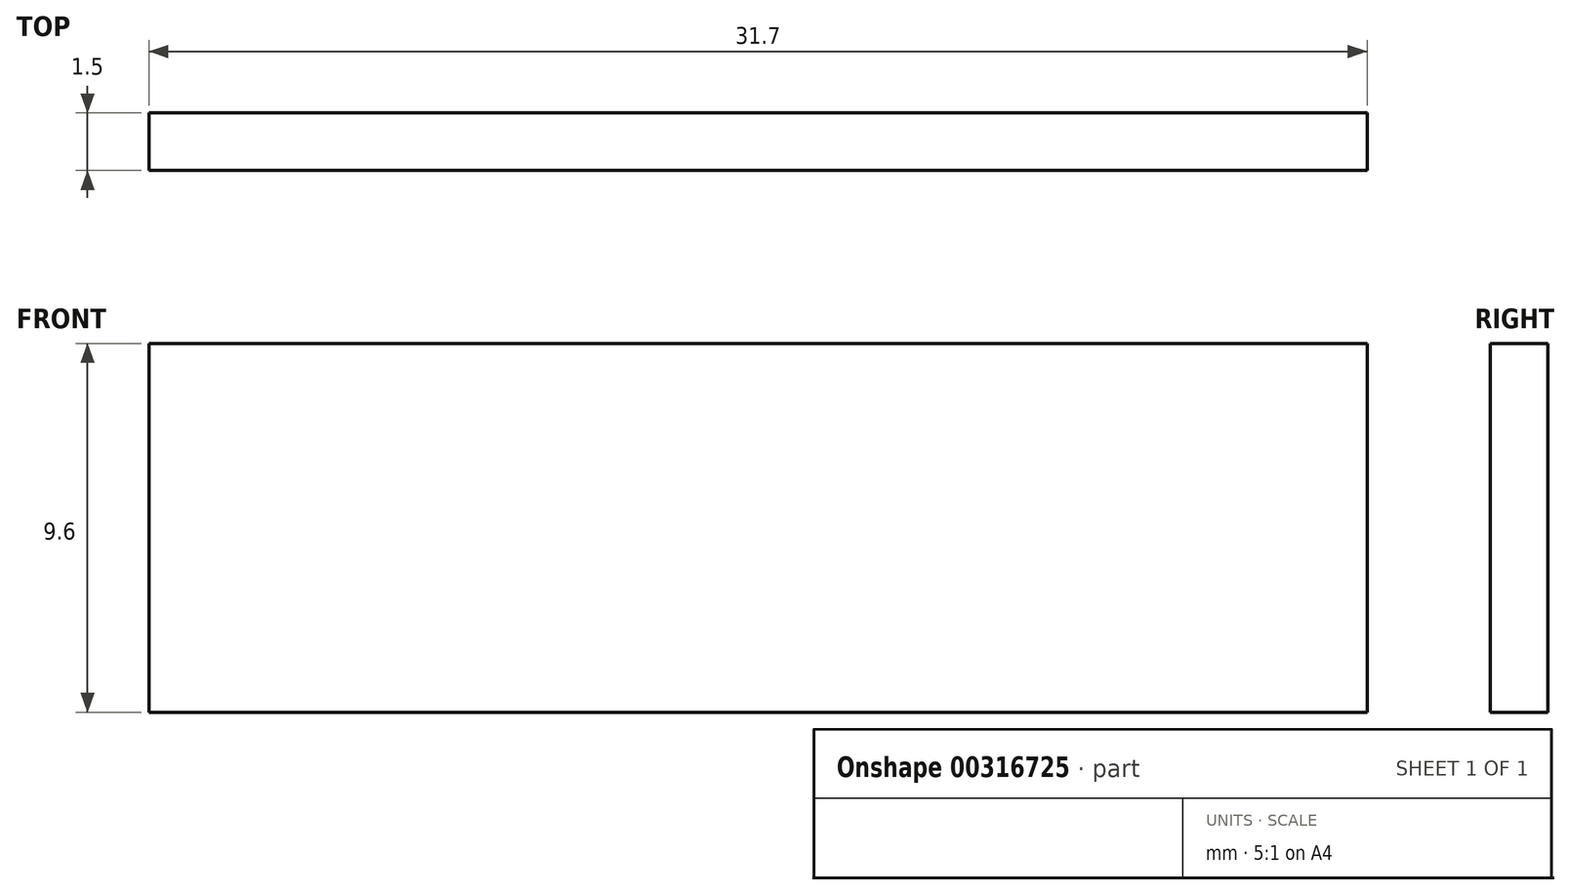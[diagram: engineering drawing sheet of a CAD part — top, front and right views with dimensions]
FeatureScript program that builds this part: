
annotation { "Feature Type Name" : "Feature", "Feature Type Description" : "" }
export const myFeature = defineFeature(function(context is Context, id is Id, definition is map)
    precondition{}
    {
        {
            var Q0;
            Q0=qCreatedBy(makeId("Front.planeOp"),FACE);
            var sketch = newSketch(context, id + "F0", { "sketchPlane" : qUnion([Q0])});
            skLineSegment(sketch, "E0.bottom", {"start": v(-51.79, 14.76) * mm, "end": v(-20.09, 14.76) * mm});
            skLineSegment(sketch, "E0.top", {"start": v(-51.79, 5.16) * mm, "end": v(-20.09, 5.16) * mm});
            skLineSegment(sketch, "E0.left", {"start": v(-51.79, 14.76) * mm, "end": v(-51.79, 5.16) * mm});
            skLineSegment(sketch, "E0.right", {"start": v(-20.09, 14.76) * mm, "end": v(-20.09, 5.16) * mm});
            skSolve(sketch);
        }
        {
            var Q0;
            Q0=makeQuery(id+"F0.imprint","IMPRINT",FACE,{"disambiguationData":[TD([[makeQuery(id+"F0.imprint","IMPRINT",EDGE,{"derivedFrom":sQuery(id+"F0.wireOp",EDGE,"E0.bottom")}),-1.0]])]});
            extrude(context, id + "F1", {"entities" : qUnion([Q0]), "depth" : 1.5 * mm});
        }
    });
